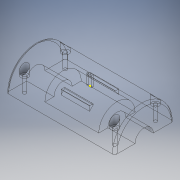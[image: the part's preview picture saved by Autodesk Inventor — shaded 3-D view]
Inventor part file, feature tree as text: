
AUTODESK INVENTOR PART (.ipt)
format: ipt  version: 2018 (Build 220112000, 112)  size: 266,240 bytes
history: native  units: in
note: dims shown in document units (in); Inventor stores cm internally (conversion verified against a paired STEP export)
features: sketch x10, extrude x9, plane x2, fillet x2, mirror x1
ambient origin geometry x8: Origin, YZ Plane, XZ Plane, XY Plane, X Axis, Y Axis, Z Axis, Center Point
bodies: Solid1 (feature_tree)
feature tree (24):
  extrude  "Extrusion1"  Depth=1.0in
  plane  "Work Plane2"
  sketch  "Sketch3"  dims[d29=0.0in d30=0.265in]
  sketch  "Sketch4"  dims[d31=0.075in d32=0.625in]
  extrude  "Extrusion3"  Depth=0.265in
  extrude  "Extrusion4"  Depth=0.625in
  extrude  "Extrusion5"  Depth=0.625in
  extrude  "Extrusion6"  Depth=1.0in
  extrude  "Extrusion7"  Depth=0.625in
  extrude  "Extrusion8"  Depth=0.5in
  extrude  "Extrusion9"  Depth=1.5in TaperAngle=0.0deg
  plane  "Work Plane3"
  extrude  "Extrusion10"  Depth=1.5in
  mirror  "Mirror3"
  fillet  "Fillet6"  Radius=1.625in
  fillet  "Fillet7"  Radius=1.5in
  sketch  "Sketch1"  dims[d6=1.9685in d7=0.0in d24=1.0in]
  sketch  "Sketch5"  dims[d34=0.59in d35=0.05in d36=0.0in d37=0.0in d40=0.625in]
  sketch  "Sketch6"  dims[d41=0.5in d42=0.0in d44=1.0in]
  sketch  "Sketch7"  dims[d45=0.625in d46=0.625in]
  sketch  "Sketch9"  dims[d51=1.125in d52=1.5in d53=0.0in]
  sketch  "Sketch10"  dims[d61=1.5748in d62=0.0in d68=0.5in d69=1.125in d70=0.5in d71=1.625in d72=1.5in d73=0.0in]
  sketch  "Sketch11"  dims[d74=0.19in d75=0.5in d76=0.5in d77=0.5in d78=0.5in d79=0.19in d80=0.5in d81=0.5in d82=0.5in d83=0.5in d84=0.19in d85=0.19in d86=1.5in d87=0.0in d88=-1.1196in d89=0.4in d90=0.3997in d91=0.4in d92=0.4in d93=0.3in d94=0.5in d95=0.0in d96=0.0in d102=135.0deg d103=0.2in d104=0.1in d105=0.3in d106=0.15in d110=1.625in d111=1.625in d112=1.625in d113=1.625in d114=0.125in d115=0.01in]
  sketch  "Sketch8"  dims[d47=0.5in d48=0.0in d50=0.5in]
